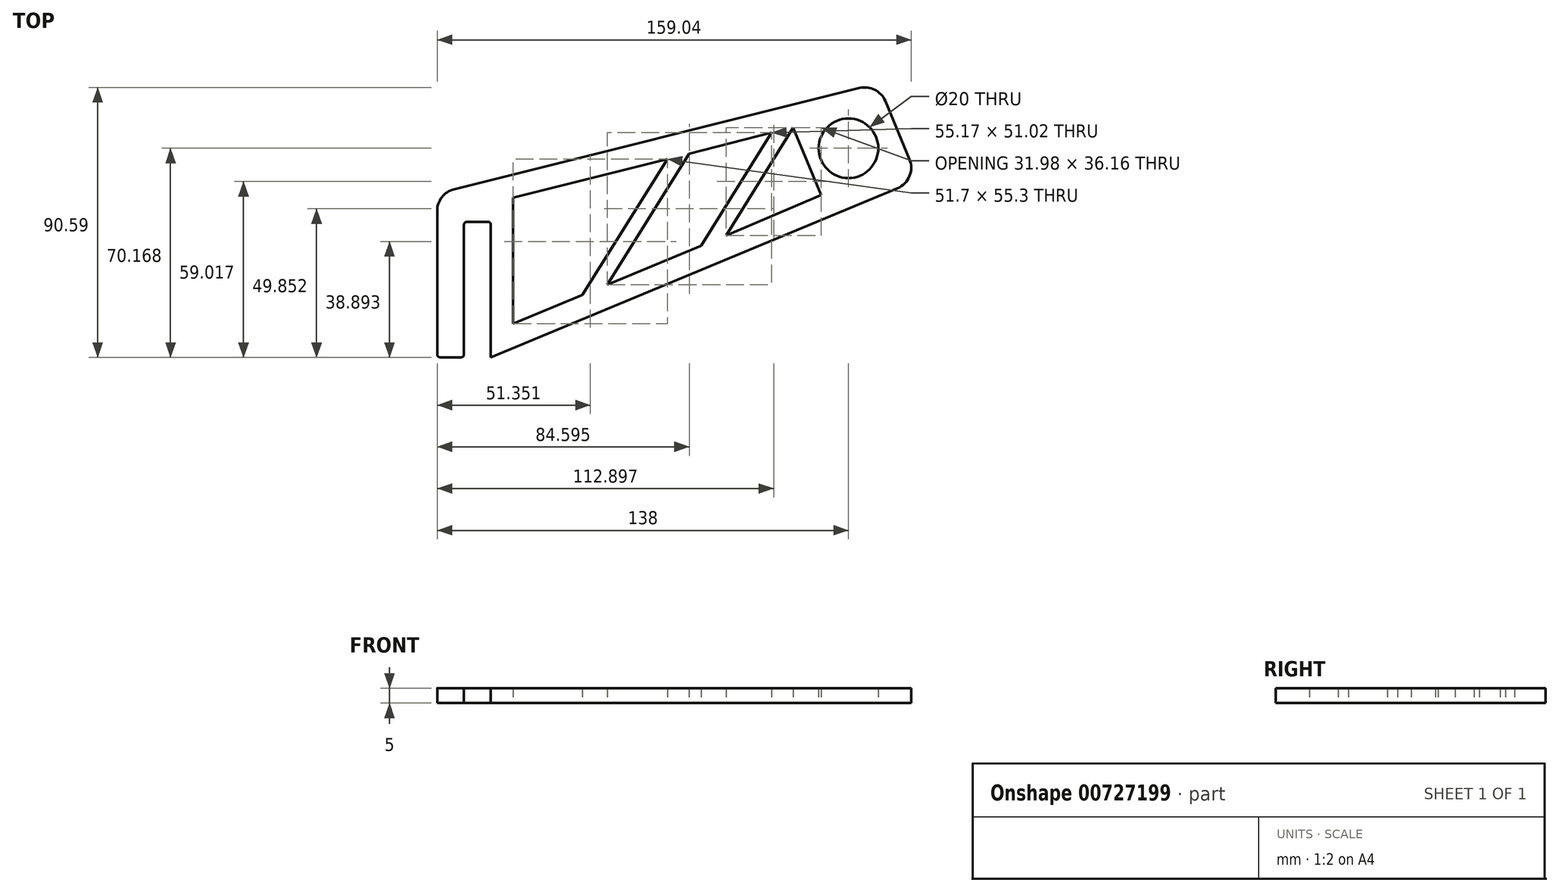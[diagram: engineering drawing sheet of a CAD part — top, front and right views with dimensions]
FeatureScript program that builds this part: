
annotation { "Feature Type Name" : "Feature", "Feature Type Description" : "" }
export const myFeature = defineFeature(function(context is Context, id is Id, definition is map)
    precondition{}
    {
        {
            var Q0;
            Q0=qCreatedBy(makeId("Top.planeOp"),FACE);
            var sketch = newSketch(context, id + "F0", { "sketchPlane" : qUnion([Q0])});
            skLineSegment(sketch, "E0", {"start": v(-78.9, 1) * mm, "end": v(-78.9, 44.5) * mm});
            skLineSegment(sketch, "E1", {"start": v(-77.9, 45.5) * mm, "end": v(-70.9, 45.5) * mm});
            skLineSegment(sketch, "E2", {"start": v(-69.9, 44.5) * mm, "end": v(-69.9, 0) * mm});
            skLineSegment(sketch, "E3", {"start": v(-69.9, 0) * mm, "end": v(66.53, 56.73) * mm});
            skLineSegment(sketch, "E4", {"start": v(70.57, 66.53) * mm, "end": v(62.5, 85.97) * mm});
            skLineSegment(sketch, "E5", {"start": v(-79.9, 0) * mm, "end": v(-86.9, 0) * mm});
            skLineSegment(sketch, "E6", {"start": v(-87.9, 1) * mm, "end": v(-87.9, 49.14) * mm});
            skLineSegment(sketch, "E7", {"start": v(53.75, 90.36) * mm, "end": v(-82.2, 56.42) * mm});
            skPoint(sketch, "E8.visualSharp", {"position": v(-78.9, 45.5) * mm});
            skArc(sketch, "E8.filletArc", {"start": v(-77.9, 45.5) * mm, "mid": v(-78.6, 45.2) * mm, "end": v(-78.9, 44.5) * mm});
            skPoint(sketch, "E9.visualSharp", {"position": v(-69.9, 45.5) * mm});
            skArc(sketch, "E9.filletArc", {"start": v(-69.9, 44.5) * mm, "mid": v(-70.18, 45.2) * mm, "end": v(-70.9, 45.5) * mm});
            skPoint(sketch, "E10.visualSharp", {"position": v(-78.9, 0) * mm});
            skArc(sketch, "E10.filletArc", {"start": v(-79.9, 0) * mm, "mid": v(-79.18, 0.3) * mm, "end": v(-78.9, 1) * mm});
            skPoint(sketch, "E11.visualSharp", {"position": v(-87.9, 0) * mm});
            skArc(sketch, "E11.filletArc", {"start": v(-87.9, 1) * mm, "mid": v(-87.6, 0.3) * mm, "end": v(-86.9, 0) * mm});
            skPoint(sketch, "E12.visualSharp", {"position": v(-69.9, 0) * mm});
            skPoint(sketch, "E13.visualSharp", {"position": v(-87.9, 55) * mm});
            skPoint(sketch, "E14.visualSharp", {"position": v(73.45, 59.6) * mm});
            skPoint(sketch, "E15.visualSharp", {"position": v(60.01, 91.93) * mm});
            skLineSegment(sketch, "E16", {"start": v(-69.9, 0) * mm, "end": v(-69.9, 59.5) * mm, "construction": true});
            skLineSegment(sketch, "E17", {"start": v(66.73, 75.77) * mm, "end": v(-69.9, 29.75) * mm, "construction": true});
            skCircle(sketch, "E18", {"center": v(50.1, 70.17) * mm, "radius": 10 * mm});
            skLineSegment(sketch, "E19", {"start": v(-62.4, 53.64) * mm, "end": v(-3.41, 68.36) * mm, "construction": true});
            skLineSegment(sketch, "E20", {"start": v(-62.4, 53.64) * mm, "end": v(-62.4, 11.24) * mm, "construction": true});
            skLineSegment(sketch, "E21", {"start": v(55.57, 83.09) * mm, "end": v(63.65, 63.65) * mm, "construction": true});
            skLineSegment(sketch, "E22", {"start": v(-3.41, 68.36) * mm, "end": v(0.63, 37.45) * mm, "construction": true});
            skLineSegment(sketch, "E23", {"start": v(0.63, 37.45) * mm, "end": v(-62.4, 11.24) * mm, "construction": true});
            skLineSegment(sketch, "E24", {"start": v(-3.41, 68.36) * mm, "end": v(55.57, 83.09) * mm, "construction": true});
            skLineSegment(sketch, "E25", {"start": v(-30.88, 24.34) * mm, "end": v(-32.9, 61) * mm, "construction": true});
            skLineSegment(sketch, "E26", {"start": v(24.29, 75.36) * mm, "end": v(30.35, 50.19) * mm, "construction": true});
            skLineSegment(sketch, "E27", {"start": v(-3.41, 68.36) * mm, "end": v(-30.88, 24.34) * mm});
            skLineSegment(sketch, "E28", {"start": v(-10.69, 66.54) * mm, "end": v(-39.18, 20.9) * mm});
            skLineSegment(sketch, "E29", {"start": v(24.29, 75.36) * mm, "end": v(0.63, 37.45) * mm});
            skLineSegment(sketch, "E30", {"start": v(31.59, 77.1) * mm, "end": v(9.02, 40.94) * mm});
            skLineSegment(sketch, "E31", {"start": v(24.29, 75.36) * mm, "end": v(-3.41, 68.36) * mm});
            skLineSegment(sketch, "E32", {"start": v(0.63, 37.45) * mm, "end": v(-30.88, 24.34) * mm});
            skLineSegment(sketch, "E33", {"start": v(-39.18, 20.9) * mm, "end": v(-62.4, 11.24) * mm});
            skLineSegment(sketch, "E34", {"start": v(-62.4, 53.64) * mm, "end": v(-62.4, 11.24) * mm});
            skLineSegment(sketch, "E35", {"start": v(-62.4, 53.64) * mm, "end": v(-10.69, 66.54) * mm});
            skLineSegment(sketch, "E36", {"start": v(31.59, 77.1) * mm, "end": v(41, 54.47) * mm});
            skLineSegment(sketch, "E37", {"start": v(63.65, 63.65) * mm, "end": v(0.63, 37.45) * mm, "construction": true});
            skLineSegment(sketch, "E38", {"start": v(9.02, 40.94) * mm, "end": v(41, 54.47) * mm});
            skArc(sketch, "E39.filletArc", {"start": v(62.5, 85.97) * mm, "mid": v(58.94, 89.79) * mm, "end": v(53.75, 90.36) * mm});
            skArc(sketch, "E40.filletArc", {"start": v(66.53, 56.73) * mm, "mid": v(70.58, 60.8) * mm, "end": v(70.57, 66.53) * mm});
            skArc(sketch, "E41.filletArc", {"start": v(-82.2, 56.42) * mm, "mid": v(-86.3, 53.76) * mm, "end": v(-87.9, 49.14) * mm});
            skSolve(sketch);
        }
        {
            var Q0;
            Q0=makeQuery(id+"F0.imprint","IMPRINT",FACE,{"disambiguationData":[TD([[makeQuery(id+"F0.imprint","IMPRINT",EDGE,{"derivedFrom":sQuery(id+"F0.wireOp",EDGE,"E0")}),1.0]])]});
            extrude(context, id + "F1", {"entities" : qUnion([Q0]), "depth" : 5 * mm, "offsetDistance" : 25 * mm});
        }
    });
